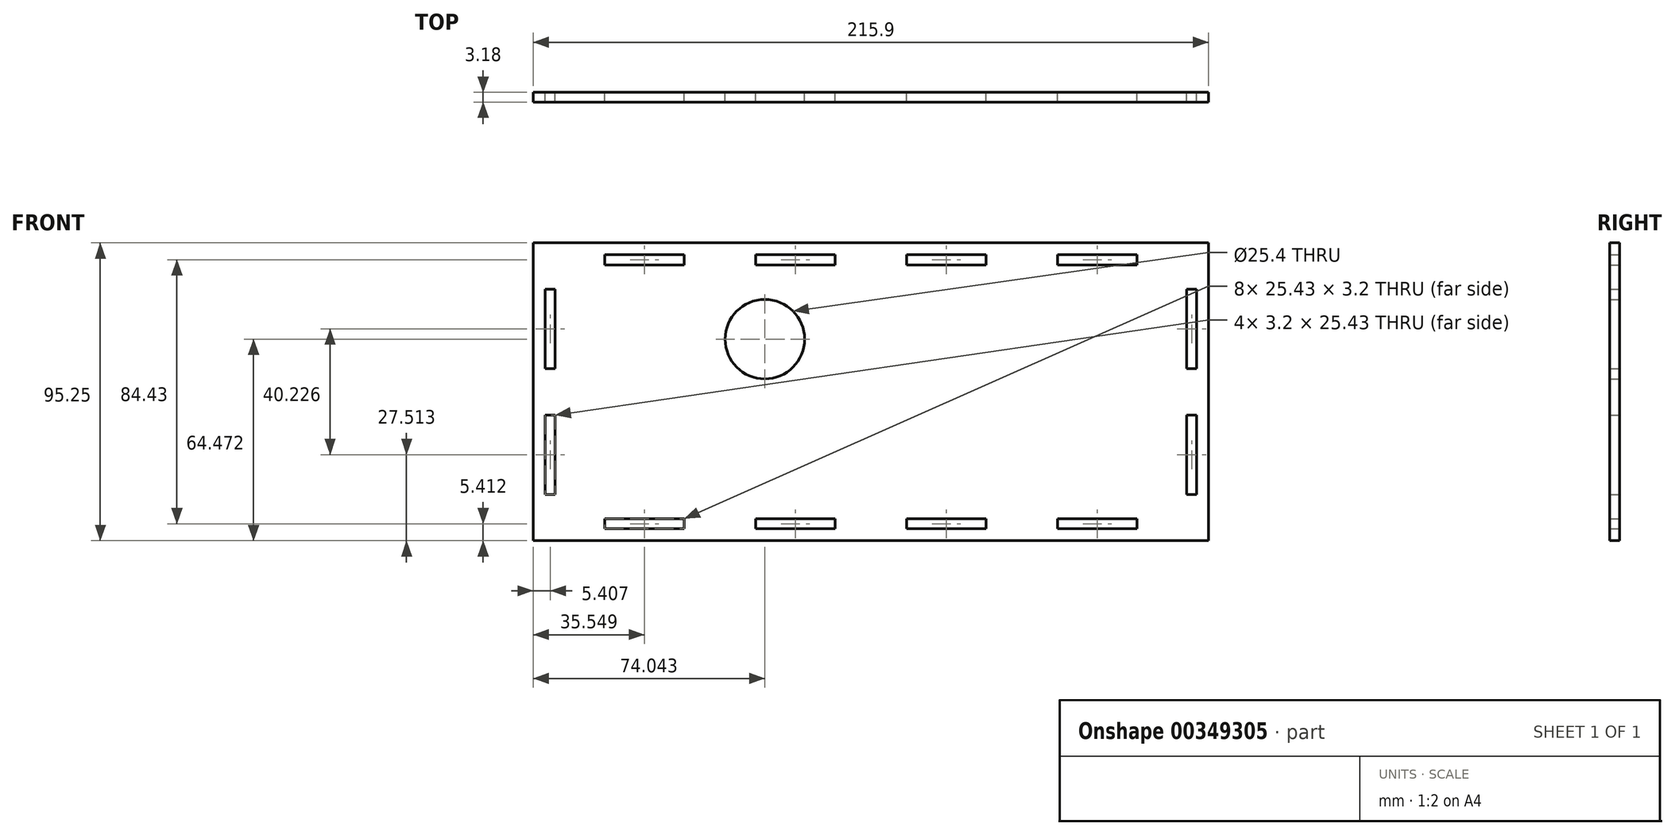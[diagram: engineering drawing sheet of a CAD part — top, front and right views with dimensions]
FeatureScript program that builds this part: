
annotation { "Feature Type Name" : "Feature", "Feature Type Description" : "" }
export const myFeature = defineFeature(function(context is Context, id is Id, definition is map)
    precondition{}
    {
        {
            var Q0;
            Q0=qCreatedBy(makeId("Front.planeOp"),FACE);
            var sketch = newSketch(context, id + "F0", { "sketchPlane" : qUnion([Q0])});
            skLineSegment(sketch, "E0.bottom", {"start": v(-97.14, 44.33) * mm, "end": v(118.76, 44.33) * mm});
            skLineSegment(sketch, "E0.top", {"start": v(-97.14, -50.92) * mm, "end": v(118.76, -50.92) * mm});
            skLineSegment(sketch, "E0.left", {"start": v(-97.14, 44.33) * mm, "end": v(-97.14, -50.92) * mm});
            skLineSegment(sketch, "E0.right", {"start": v(118.76, 44.33) * mm, "end": v(118.76, -50.92) * mm});
            skCircle(sketch, "E1", {"center": v(-23.1, 13.55) * mm, "radius": 12.7 * mm});
            skLineSegment(sketch, "E2.bottom", {"start": v(-74.3, 40.52) * mm, "end": v(-48.88, 40.52) * mm});
            skLineSegment(sketch, "E2.top", {"start": v(-74.3, 37.32) * mm, "end": v(-48.88, 37.32) * mm});
            skLineSegment(sketch, "E2.left", {"start": v(-74.3, 40.52) * mm, "end": v(-74.3, 37.32) * mm});
            skLineSegment(sketch, "E2.right", {"start": v(-48.88, 40.52) * mm, "end": v(-48.88, 37.32) * mm});
            skLineSegment(sketch, "E3.bottom", {"start": v(-26.04, 40.52) * mm, "end": v(-0.61, 40.52) * mm});
            skLineSegment(sketch, "E3.top", {"start": v(-26.04, 37.32) * mm, "end": v(-0.61, 37.32) * mm});
            skLineSegment(sketch, "E3.left", {"start": v(-26.04, 40.52) * mm, "end": v(-26.04, 37.32) * mm});
            skLineSegment(sketch, "E3.right", {"start": v(-0.61, 40.52) * mm, "end": v(-0.61, 37.32) * mm});
            skLineSegment(sketch, "E4.bottom", {"start": v(70.5, 40.52) * mm, "end": v(95.92, 40.52) * mm});
            skLineSegment(sketch, "E4.top", {"start": v(70.5, 37.32) * mm, "end": v(95.92, 37.32) * mm});
            skLineSegment(sketch, "E4.left", {"start": v(70.5, 40.52) * mm, "end": v(70.5, 37.32) * mm});
            skLineSegment(sketch, "E4.right", {"start": v(95.92, 40.52) * mm, "end": v(95.92, 37.32) * mm});
            skLineSegment(sketch, "E5.bottom", {"start": v(22.23, 40.52) * mm, "end": v(47.65, 40.52) * mm});
            skLineSegment(sketch, "E5.top", {"start": v(22.23, 37.32) * mm, "end": v(47.65, 37.32) * mm});
            skLineSegment(sketch, "E5.left", {"start": v(22.23, 40.52) * mm, "end": v(22.23, 37.32) * mm});
            skLineSegment(sketch, "E5.right", {"start": v(47.65, 40.52) * mm, "end": v(47.65, 37.32) * mm});
            skLineSegment(sketch, "E6.bottom", {"start": v(-74.3, -43.9) * mm, "end": v(-48.88, -43.9) * mm});
            skLineSegment(sketch, "E6.top", {"start": v(-74.3, -47.1) * mm, "end": v(-48.88, -47.1) * mm});
            skLineSegment(sketch, "E6.left", {"start": v(-74.3, -43.9) * mm, "end": v(-74.3, -47.1) * mm});
            skLineSegment(sketch, "E6.right", {"start": v(-48.88, -43.9) * mm, "end": v(-48.88, -47.1) * mm});
            skLineSegment(sketch, "E7.bottom", {"start": v(-26.04, -43.9) * mm, "end": v(-0.61, -43.9) * mm});
            skLineSegment(sketch, "E7.top", {"start": v(-26.04, -47.1) * mm, "end": v(-0.61, -47.1) * mm});
            skLineSegment(sketch, "E7.left", {"start": v(-26.04, -43.9) * mm, "end": v(-26.04, -47.1) * mm});
            skLineSegment(sketch, "E7.right", {"start": v(-0.61, -43.9) * mm, "end": v(-0.61, -47.1) * mm});
            skLineSegment(sketch, "E8.bottom", {"start": v(70.5, -43.9) * mm, "end": v(95.92, -43.9) * mm});
            skLineSegment(sketch, "E8.top", {"start": v(70.5, -47.1) * mm, "end": v(95.92, -47.1) * mm});
            skLineSegment(sketch, "E8.left", {"start": v(70.5, -43.9) * mm, "end": v(70.5, -47.1) * mm});
            skLineSegment(sketch, "E8.right", {"start": v(95.92, -43.9) * mm, "end": v(95.92, -47.1) * mm});
            skLineSegment(sketch, "E9.bottom", {"start": v(22.23, -43.9) * mm, "end": v(47.65, -43.9) * mm});
            skLineSegment(sketch, "E9.top", {"start": v(22.23, -47.1) * mm, "end": v(47.65, -47.1) * mm});
            skLineSegment(sketch, "E9.left", {"start": v(22.23, -43.9) * mm, "end": v(22.23, -47.1) * mm});
            skLineSegment(sketch, "E9.right", {"start": v(47.65, -43.9) * mm, "end": v(47.65, -47.1) * mm});
            skLineSegment(sketch, "E10.bottom", {"start": v(111.75, 29.53) * mm, "end": v(114.95, 29.53) * mm});
            skLineSegment(sketch, "E10.top", {"start": v(111.75, 4.1) * mm, "end": v(114.95, 4.1) * mm});
            skLineSegment(sketch, "E10.left", {"start": v(111.75, 29.53) * mm, "end": v(111.75, 4.1) * mm});
            skLineSegment(sketch, "E10.right", {"start": v(114.95, 29.53) * mm, "end": v(114.95, 4.1) * mm});
            skLineSegment(sketch, "E11.bottom", {"start": v(111.75, -10.7) * mm, "end": v(114.95, -10.7) * mm});
            skLineSegment(sketch, "E11.top", {"start": v(111.75, -36.12) * mm, "end": v(114.95, -36.12) * mm});
            skLineSegment(sketch, "E11.left", {"start": v(111.75, -10.7) * mm, "end": v(111.75, -36.12) * mm});
            skLineSegment(sketch, "E11.right", {"start": v(114.95, -10.7) * mm, "end": v(114.95, -36.12) * mm});
            skLineSegment(sketch, "E12.bottom", {"start": v(-93.33, 29.53) * mm, "end": v(-90.13, 29.53) * mm});
            skLineSegment(sketch, "E12.top", {"start": v(-93.33, 4.1) * mm, "end": v(-90.13, 4.1) * mm});
            skLineSegment(sketch, "E12.left", {"start": v(-93.33, 29.53) * mm, "end": v(-93.33, 4.1) * mm});
            skLineSegment(sketch, "E12.right", {"start": v(-90.13, 29.53) * mm, "end": v(-90.13, 4.1) * mm});
            skLineSegment(sketch, "E13.bottom", {"start": v(-93.33, -10.7) * mm, "end": v(-90.13, -10.7) * mm});
            skLineSegment(sketch, "E13.top", {"start": v(-93.33, -36.12) * mm, "end": v(-90.13, -36.12) * mm});
            skLineSegment(sketch, "E13.left", {"start": v(-93.33, -10.7) * mm, "end": v(-93.33, -36.12) * mm});
            skLineSegment(sketch, "E13.right", {"start": v(-90.13, -10.7) * mm, "end": v(-90.13, -36.12) * mm});
            skSolve(sketch);
        }
        {
            var Q0;
            Q0=makeQuery(id+"F0.imprint","IMPRINT",FACE,{"disambiguationData":[TD([[makeQuery(id+"F0.imprint","IMPRINT",EDGE,{"derivedFrom":sQuery(id+"F0.wireOp",EDGE,"E0.bottom")}),-1.0]])]});
            extrude(context, id + "F1", {"entities" : qUnion([Q0]), "depth" : 3.17 * mm});
        }
    });
